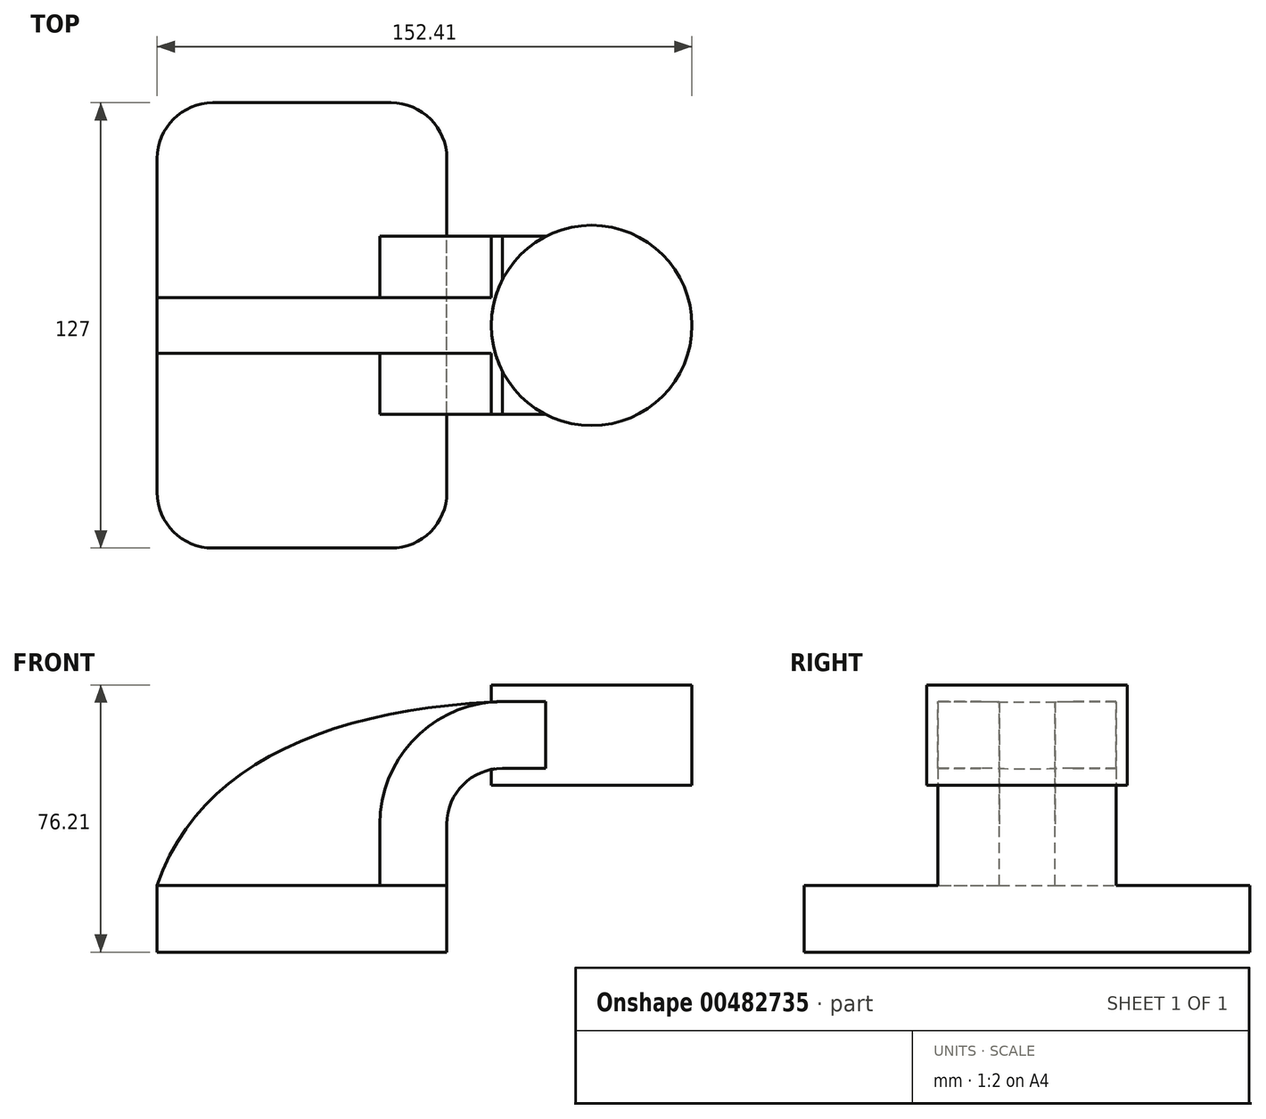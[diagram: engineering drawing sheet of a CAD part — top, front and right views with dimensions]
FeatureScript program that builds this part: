
annotation { "Feature Type Name" : "Feature", "Feature Type Description" : "" }
export const myFeature = defineFeature(function(context is Context, id is Id, definition is map)
    precondition{}
    {
        {
            var Q0;
            Q0=qCreatedBy(makeId("Front.planeOp"),FACE);
            var sketch = newSketch(context, id + "F0", { "sketchPlane" : qUnion([Q0])});
            skLineSegment(sketch, "E0.bottom", {"start": v(-41.28, 9.52) * mm, "end": v(41.27, 9.53) * mm});
            skLineSegment(sketch, "E0.top", {"start": v(-41.28, -9.53) * mm, "end": v(41.28, -9.53) * mm});
            skLineSegment(sketch, "E0.left", {"start": v(-41.28, 9.52) * mm, "end": v(-41.27, -9.53) * mm});
            skLineSegment(sketch, "E0.right", {"start": v(41.28, 9.53) * mm, "end": v(41.28, -9.52) * mm});
            skPoint(sketch, "E0.middle", {"position": v(0, 0) * mm});
            skLineSegment(sketch, "E1.bottom", {"start": v(111.12, 38.1) * mm, "end": v(60.32, 38.1) * mm});
            skLineSegment(sketch, "E1.top", {"start": v(111.12, 66.68) * mm, "end": v(60.32, 66.68) * mm});
            skLineSegment(sketch, "E1.left", {"start": v(111.12, 38.1) * mm, "end": v(111.12, 66.68) * mm});
            skLineSegment(sketch, "E1.right", {"start": v(60.32, 38.1) * mm, "end": v(60.32, 66.67) * mm});
            skPoint(sketch, "E1.middle", {"position": v(85.72, 52.39) * mm});
            skLineSegment(sketch, "E2", {"start": v(41.27, 9.53) * mm, "end": v(41.27, 27) * mm});
            skArc(sketch, "E3", {"start": v(41.27, 27) * mm, "mid": v(45.92, 38.23) * mm, "end": v(57.15, 42.88) * mm});
            skLineSegment(sketch, "E4", {"start": v(57.15, 42.88) * mm, "end": v(82.55, 42.88) * mm});
            skLineSegment(sketch, "E5.0", {"start": v(57.15, 61.93) * mm, "end": v(82.55, 61.93) * mm});
            skArc(sketch, "E5.1", {"start": v(22.22, 27) * mm, "mid": v(32.45, 51.7) * mm, "end": v(57.15, 61.93) * mm});
            skLineSegment(sketch, "E5.2", {"start": v(22.22, 9.53) * mm, "end": v(22.22, 27) * mm});
            skLineSegment(sketch, "E6", {"start": v(82.55, 61.93) * mm, "end": v(82.55, 38.1) * mm});
            skLineSegment(sketch, "E7", {"start": v(82.55, 66.68) * mm, "end": v(82.55, 61.93) * mm});
            skFitSpline(sketch, "E8", {"points": [v(-41.28, 9.52) * mm, v(57.15, 61.93) * mm], "startDerivative": vector(35.66, 104.03) * mm, "endDerivative": vector(147.26, 5.9) * mm});
            skSolve(sketch);
        }
        {
            var Q0;
            Q0=makeQuery(id+"F0.imprint","IMPRINT",FACE,{"disambiguationData":[TD([[makeQuery(id+"F0.imprint","IMPRINT",EDGE,{"derivedFrom":sQuery(id+"F0.wireOp",EDGE,"E0.top")}),1.0]])]});
            extrude(context, id + "F1", {"entities" : qUnion([Q0]), "endBound" : BoundingType.SYMMETRIC, "depth" : 127 * mm});
        }
        {
            var Q0;
            {var subQ1=sQuery(id+"F0.wireOp",EDGE,"E2");Q0=makeQuery(id+"F0.imprint","IMPRINT",FACE,{"disambiguationData":[TD([[makeQuery(id+"F0.imprint","IMPRINT",EDGE,{"derivedFrom":subQ1}),1.0]])]});}
            var Q1;
            {var subQ0=sQuery(id+"F0.wireOp",EDGE,"E4");var subQ1=sQuery(id+"F0.wireOp",EDGE,"E1.right");var subQ2=makeQuery(id+"F0.imprint","INTERSECT",VERTEX,{"derivedFrom":[subQ1,subQ0]});Q1=makeQuery(id+"F0.imprint","IMPRINT",FACE,{"disambiguationData":[TD([[makeQuery(id+"F0.imprint","IMPRINT",EDGE,{"disambiguationData":[TD([[subQ2,-1.0]])],"derivedFrom":subQ1}),-1.0]])]});}
            extrude(context, id + "F2", {"entities" : qUnion([Q0, Q1]), "operationType" : NewBodyOperationType.ADD, "endBound" : BoundingType.SYMMETRIC, "depth" : 50.8 * mm});
        }
        {
            var Q0;
            {var subQ3=sQuery(id+"F0.wireOp",EDGE,"E5.2");Q0=makeQuery(id+"F0.imprint","IMPRINT",FACE,{"disambiguationData":[TD([[makeQuery(id+"F0.imprint","IMPRINT",EDGE,{"derivedFrom":subQ3}),1.0]])]});}
            extrude(context, id + "F3", {"entities" : qUnion([Q0]), "operationType" : NewBodyOperationType.ADD, "endBound" : BoundingType.SYMMETRIC, "depth" : 15.88 * mm});
        }
        {
            var Q0;
            {var subQ0=sQuery(id+"F0.wireOp",EDGE,"E1.left");Q0=makeQuery(id+"F0.imprint","IMPRINT",FACE,{"disambiguationData":[TD([[makeQuery(id+"F0.imprint","IMPRINT",EDGE,{"derivedFrom":subQ0}),1.0]])]});}
            var Q1;
            Q1=sQuery(id+"F0.wireOp",EDGE,"E6");
            revolve(context, id + "F4", {"operationType" : NewBodyOperationType.ADD, "entities" : qUnion([Q0]), "axis" : qUnion([Q1]), "revolveType" : RevolveType.FULL});
        }
        {
            var Q0;
            Q0=makeQuery(id+"F1.opExtrude","CAP_EDGE",EDGE,{"disambiguationData":[OSD([sQuery(id+"F0.wireOp",EDGE,"E0.left")])],"isStart":false});
            var Q1;
            Q1=makeQuery(id+"F1.opExtrude","CAP_EDGE",EDGE,{"disambiguationData":[OSD([sQuery(id+"F0.wireOp",EDGE,"E0.right")])],"isStart":false});
            var Q2;
            Q2=makeQuery(id+"F1.opExtrude","CAP_EDGE",EDGE,{"disambiguationData":[OSD([sQuery(id+"F0.wireOp",EDGE,"E0.right")])],"isStart":true});
            var Q3;
            Q3=makeQuery(id+"F1.opExtrude","CAP_EDGE",EDGE,{"disambiguationData":[OSD([sQuery(id+"F0.wireOp",EDGE,"E0.left")])],"isStart":true});
            fillet(context, id + "F5", {"entities" : qUnion([Q0, Q1, Q2, Q3]), "radius" : 15.88 * mm, "tangentPropagation" : true, "allowEdgeOverflow" : false});
        }
    });
